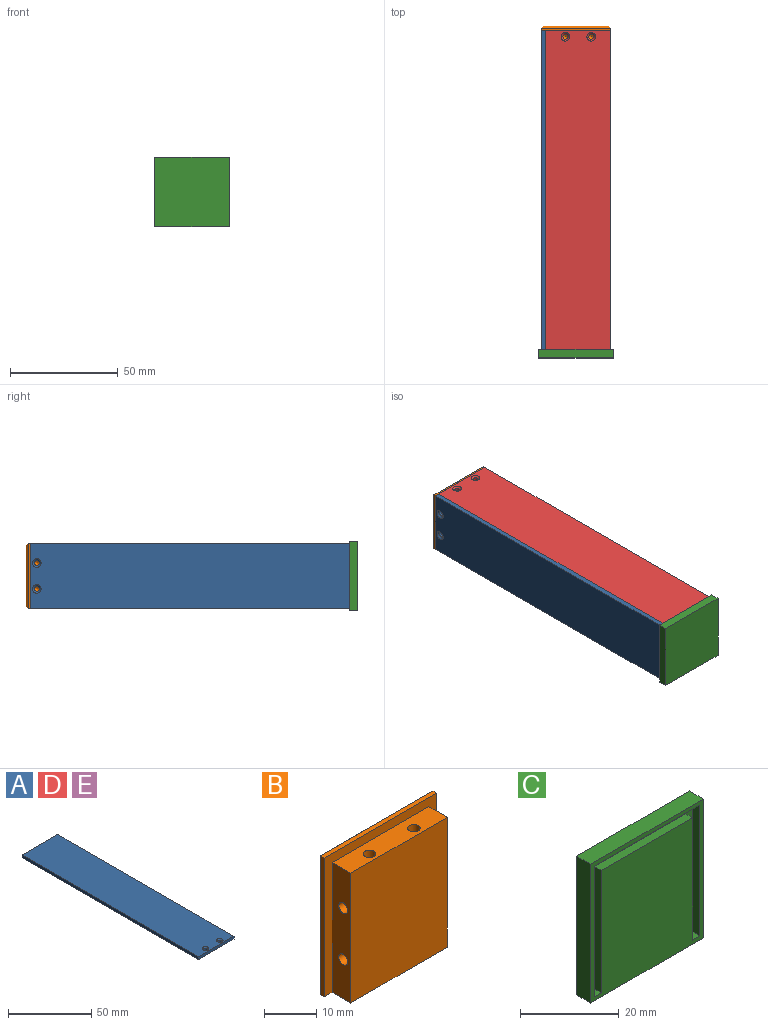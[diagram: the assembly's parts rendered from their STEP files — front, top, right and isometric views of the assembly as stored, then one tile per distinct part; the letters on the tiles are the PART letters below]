
ASSEMBLY  parts=5 mates=5
PART A: 10 faces, bbox 30.3x150x2.1 mm
  f0: plane 30.3x2.1mm, normal (0,1,0), area 63.6mm2, adj f1,f3,f4,f5
  f1: plane 150x2.1mm, normal (-1,0,0), area 315mm2, adj f0,f2,f4,f5
  f2: plane 30.3x2.1mm, normal (0,-1,0), area 63.6mm2, adj f1,f3,f4,f5
  f3: plane 150x2.1mm, normal (1,0,0), area 315mm2, adj f0,f2,f4,f5
  f4: plane 150x30.3mm, normal (0,0,1), area 4519.9mm2, adj f0,f1,f2,f3,f7,f9
  f5: plane 150x30.3mm, normal (0,0,-1), area 4536mm2, adj f0,f1,f2,f3,f6,f8
  f6: cylinder r=1.2mm len=2.4mm, axis (0,0,1), area 9.8mm2, adj f5,f7
  f7: cone r=1.2mm half-angle=45deg, axis (0,0,1), area 11.4mm2, adj f4,f6
  f8: cylinder r=1.2mm len=2.4mm, axis (0,0,1), area 9.8mm2, adj f5,f9
  f9: cone r=1.2mm half-angle=45deg, axis (0,0,1), area 11.4mm2, adj f4,f8
PART B: 26 faces, bbox 30.3x7x32.4 mm
  f0: plane 32.4x30.3mm, normal (0,-1,0), area 190.9mm2, adj f1,f2,f3,f4,f6,f7,f8
  f1: plane 30.3x1mm, normal (0,0,1), area 30.3mm2, adj f0,f2,f4,f23
  f2: plane 32.4x1mm, normal (-1,0,0), area 32.4mm2, adj f0,f1,f3,f22
  f3: plane 30.3x6mm, normal (0,0,-1), area 160.8mm2, adj f0,f2,f4,f6,f8,f9,f24
  f4: plane 32.4x1mm, normal (1,0,0), area 32.4mm2, adj f0,f1,f3,f25
  f5: plane 30.4x28.3mm, normal (0,1,0), area 860.3mm2, adj f22,f23,f24,f25
  f6: plane 30.3x5mm, normal (1,0,0), area 142.5mm2, adj f0,f3,f7,f9,f19,f21
  f7: plane 26.1x5mm, normal (0,0,1), area 121.5mm2, adj f0,f6,f8,f9,f15,f17
  f8: plane 30.3x5mm, normal (-1,0,0), area 142.5mm2, adj f0,f3,f7,f9,f11,f13
  f9: plane 30.3x26.1mm, normal (0,-1,0), area 790.8mm2, adj f3,f6,f7,f8
  f10: cone r=0mm half-angle=59deg, axis (-1,0,0), area 5.3mm2, adj f11
  f11: cylinder r=1.2mm len=6mm, axis (-1,0,0), area 45.2mm2, adj f8,f10
  f12: cone r=0mm half-angle=59deg, axis (-1,0,0), area 5.3mm2, adj f13
  f13: cylinder r=1.2mm len=6mm, axis (-1,0,0), area 45.2mm2, adj f8,f12
  f14: cone r=0mm half-angle=59deg, axis (0,0,1), area 5.3mm2, adj f15
  f15: cylinder r=1.2mm len=6mm, axis (0,0,1), area 45.2mm2, adj f7,f14
  f16: cone r=0mm half-angle=59deg, axis (0,0,1), area 5.3mm2, adj f17
  f17: cylinder r=1.2mm len=6mm, axis (0,0,1), area 45.2mm2, adj f7,f16
  f18: cone r=0mm half-angle=59deg, axis (1,0,0), area 5.3mm2, adj f19
  f19: cylinder r=1.2mm len=6mm, axis (1,0,0), area 45.2mm2, adj f6,f18
  f20: cone r=0mm half-angle=59deg, axis (1,0,0), area 5.3mm2, adj f21
  f21: cylinder r=1.2mm len=6mm, axis (1,0,0), area 45.2mm2, adj f6,f20
  f22: plane 32.4x1mm, normal (-0.71,0.71,0), area 44.4mm2, adj f2,f5,f23,f24
  f23: plane 30.3x1mm, normal (0,0.71,0.71), area 41.4mm2, adj f1,f5,f22,f25
  f24: plane 30.3x1mm, normal (0,0.71,-0.71), area 41.4mm2, adj f3,f5,f22,f25
  f25: plane 32.4x1mm, normal (0.71,0.71,0), area 44.4mm2, adj f4,f5,f23,f24
PART C: 15 faces, bbox 32.3x4x34.4 mm
  f0: plane 32.3x4mm, normal (0,0,1), area 129.2mm2, adj f1,f3,f4,f5
  f1: plane 34.4x4mm, normal (-1,0,0), area 137.6mm2, adj f0,f2,f4,f5
  f2: plane 32.3x4mm, normal (0,0,-1), area 129.2mm2, adj f1,f3,f4,f5
  f3: plane 34.4x4mm, normal (1,0,0), area 137.6mm2, adj f0,f2,f4,f5
  f4: plane 34.4x32.3mm, normal (0,-1,0), area 920.2mm2, adj f0,f1,f2,f3,f6,f7,f8,f9
  f5: plane 34.4x32.3mm, normal (0,1,0), area 1111.1mm2, adj f0,f1,f2,f3
  f6: plane 30.3x2mm, normal (0,0,-1), area 60.6mm2, adj f4,f7,f13,f14
  f7: plane 32.4x2mm, normal (1,0,0), area 64.8mm2, adj f4,f6,f8,f14
  f8: plane 2.1x2mm, normal (0,0,1), area 4.2mm2, adj f4,f7,f9,f14
  f9: plane 30.3x2mm, normal (-1,0,0), area 60.6mm2, adj f4,f8,f10,f14
  f10: plane 26.1x2mm, normal (0,0,1), area 52.2mm2, adj f4,f9,f11,f14
  f11: plane 30.3x2mm, normal (1,0,0), area 60.6mm2, adj f4,f10,f12,f14
  f12: plane 2.1x2mm, normal (0,0,1), area 4.2mm2, adj f4,f11,f13,f14
  f13: plane 32.4x2mm, normal (-1,0,0), area 64.8mm2, adj f4,f6,f12,f14
  f14: plane 32.4x30.3mm, normal (0,-1,0), area 190.9mm2, adj f6,f7,f8,f9,f10,f11,f12,f13
PART D: same geometry as A
PART E: same geometry as A
PLACE A rot(axis=(0.71,0,-0.71),180deg) t=(37.16,77.61,-7.51)mm
PLACE B rot(axis=(0,-1,0),90deg) t=(67.46,229.61,7.64)mm
PLACE C rot(axis=(0.71,0,-0.71),180deg) t=(68.46,75.61,-23.66)mm
PLACE D rot(axis=(0,0,-1),180deg) t=(52.31,77.61,5.54)mm
PLACE E rot(axis=(1,0,0),180deg) t=(52.31,77.61,-20.56)mm
MATE fastened A.f2 <-> B.f0  axis (0,1,0) through (37.16,227.61,-7.51)mm
MATE planar A.f5 <-> B.f7  axis (1,0,0) through (37.16,152.47,-7.51)mm
MATE fastened D.f5 <-> B.f6  axis (0,0,-1) through (52.31,227.61,5.54)mm
MATE fastened A.f0 <-> C.f14  axis (0,-1,0) through (35.06,77.61,-7.51)mm
MATE fastened B.f8 <-> E.f5  axis (0,0,-1) through (52.31,227.61,-20.56)mm
